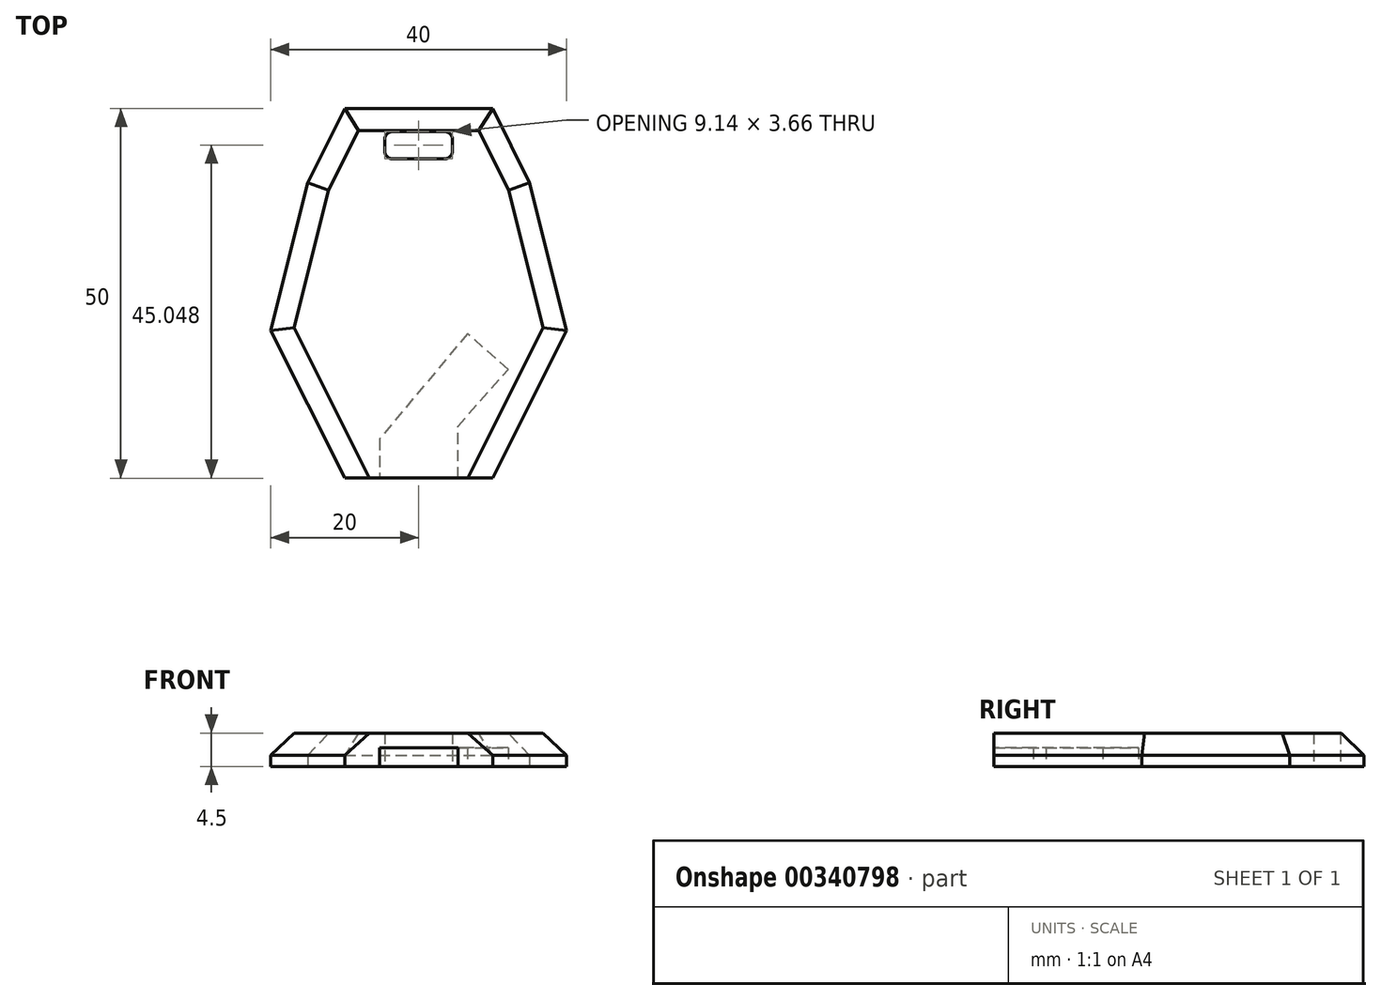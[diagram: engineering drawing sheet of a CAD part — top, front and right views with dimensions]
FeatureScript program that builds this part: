
annotation { "Feature Type Name" : "Feature", "Feature Type Description" : "" }
export const myFeature = defineFeature(function(context is Context, id is Id, definition is map)
    precondition{}
    {
        {
            var Q0;
            Q0=qCreatedBy(makeId("Top.planeOp"),FACE);
            var sketch = newSketch(context, id + "F0", { "sketchPlane" : qUnion([Q0])});
            skLineSegment(sketch, "E0", {"start": v(0, 36.91) * mm, "end": v(0, -33.24) * mm, "construction": true});
            skLineSegment(sketch, "E1", {"start": v(-15, 26.91) * mm, "end": v(15, 26.91) * mm, "construction": true});
            skLineSegment(sketch, "E2", {"start": v(-20, 6.91) * mm, "end": v(20, 6.91) * mm, "construction": true});
            skLineSegment(sketch, "E3", {"start": v(-10, 36.91) * mm, "end": v(-15, 26.91) * mm});
            skLineSegment(sketch, "E4", {"start": v(-15, 26.91) * mm, "end": v(-20, 6.91) * mm});
            skLineSegment(sketch, "E5", {"start": v(-20, 6.91) * mm, "end": v(-10, -13.09) * mm});
            skLineSegment(sketch, "E6", {"start": v(10, -13.09) * mm, "end": v(20, 6.91) * mm});
            skLineSegment(sketch, "E7", {"start": v(10, 36.91) * mm, "end": v(15, 26.91) * mm});
            skLineSegment(sketch, "E8", {"start": v(15, 26.91) * mm, "end": v(20, 6.91) * mm});
            skLineSegment(sketch, "E9", {"start": v(-10, 36.91) * mm, "end": v(10, 36.91) * mm});
            skLineSegment(sketch, "E10", {"start": v(-10, -13.09) * mm, "end": v(10, -13.09) * mm});
            skPoint(sketch, "E11", {"position": v(5.87, 6.91) * mm});
            skLineSegment(sketch, "E12", {"start": v(5.3, -13.09) * mm, "end": v(5.3, -6.09) * mm});
            skLineSegment(sketch, "E13", {"start": v(5.3, -6.09) * mm, "end": v(12.1, 1.64) * mm});
            skLineSegment(sketch, "E14", {"start": v(12.1, 1.64) * mm, "end": v(6.63, 6.47) * mm});
            skLineSegment(sketch, "E15", {"start": v(6.63, 6.47) * mm, "end": v(-5.3, -7.79) * mm});
            skLineSegment(sketch, "E16.bottom", {"start": v(-4.57, 33.79) * mm, "end": v(4.57, 33.79) * mm});
            skLineSegment(sketch, "E16.top", {"start": v(-4.57, 30.13) * mm, "end": v(4.57, 30.13) * mm});
            skLineSegment(sketch, "E16.left", {"start": v(-4.57, 33.79) * mm, "end": v(-4.57, 30.13) * mm});
            skLineSegment(sketch, "E16.right", {"start": v(4.57, 33.79) * mm, "end": v(4.57, 30.13) * mm});
            skPoint(sketch, "E16.middle", {"position": v(0, 31.96) * mm});
            skLineSegment(sketch, "E17", {"start": v(-5.3, -7.79) * mm, "end": v(-5.3, -13.09) * mm});
            skSolve(sketch);
        }
        {
            var Q0;
            Q0=makeQuery(id+"F0.imprint","IMPRINT",FACE,{"disambiguationData":[TD([[makeQuery(id+"F0.imprint","IMPRINT",EDGE,{"derivedFrom":sQuery(id+"F0.wireOp",EDGE,"E3")}),1.0]])]});
            extrude(context, id + "F1", {"entities" : qUnion([Q0]), "depth" : 4.5 * mm});
        }
        {
            var Q0;
            Q0=makeQuery(id+"F1.opExtrude","CAP_FACE",FACE,{"disambiguationData":[OSD([sQuery(id+"F0.wireOp",EDGE,"E3"),sQuery(id+"F0.wireOp",EDGE,"E4"),sQuery(id+"F0.wireOp",EDGE,"E5"),sQuery(id+"F0.wireOp",EDGE,"E6"),sQuery(id+"F0.wireOp",EDGE,"E7"),sQuery(id+"F0.wireOp",EDGE,"E8"),sQuery(id+"F0.wireOp",EDGE,"E9"),sQuery(id+"F0.wireOp",EDGE,"E10"),sQuery(id+"F0.wireOp",EDGE,"E12"),sQuery(id+"F0.wireOp",EDGE,"E13"),sQuery(id+"F0.wireOp",EDGE,"E14"),sQuery(id+"F0.wireOp",EDGE,"E15"),sQuery(id+"F0.wireOp",EDGE,"E16.bottom"),sQuery(id+"F0.wireOp",EDGE,"E16.top"),sQuery(id+"F0.wireOp",EDGE,"E16.left"),sQuery(id+"F0.wireOp",EDGE,"E16.right"),sQuery(id+"F0.wireOp",EDGE,"E17")])],"isStart":false});
            var sketch = newSketch(context, id + "F2", { "sketchPlane" : qUnion([Q0])});
            skLineSegment(sketch, "E18", {"start": v(-5.3, -13.09) * mm, "end": v(5.3, -13.09) * mm});
            skSolve(sketch);
        }
        {
            var Q0;
            Q0=makeQuery(id+"F2.imprint","IMPRINT",FACE,{"disambiguationData":[TD([[makeQuery(id+"F2.imprint","IMPRINT",EDGE,{"derivedFrom":sQuery(id+"F2.wireOp",EDGE,"E18")}),1.0]])]});
            extrude(context, id + "F3", {"entities" : qUnion([Q0]), "operationType" : NewBodyOperationType.ADD, "oppositeDirection" : true, "depth" : 2 * mm});
        }
        {
            var Q0;
            Q0=makeQuery(id+"F1.opExtrude","CAP_EDGE",EDGE,{"disambiguationData":[OSD([sQuery(id+"F0.wireOp",EDGE,"E6")])],"isStart":false});
            var Q1;
            Q1=makeQuery(id+"F1.opExtrude","CAP_EDGE",EDGE,{"disambiguationData":[OSD([sQuery(id+"F0.wireOp",EDGE,"E8")])],"isStart":false});
            var Q2;
            Q2=makeQuery(id+"F1.opExtrude","CAP_EDGE",EDGE,{"disambiguationData":[OSD([sQuery(id+"F0.wireOp",EDGE,"E5")])],"isStart":false});
            var Q3;
            Q3=makeQuery(id+"F1.opExtrude","CAP_EDGE",EDGE,{"disambiguationData":[OSD([sQuery(id+"F0.wireOp",EDGE,"E4")])],"isStart":false});
            var Q4;
            Q4=makeQuery(id+"F1.opExtrude","CAP_EDGE",EDGE,{"disambiguationData":[OSD([sQuery(id+"F0.wireOp",EDGE,"E3")])],"isStart":false});
            var Q5;
            Q5=makeQuery(id+"F1.opExtrude","CAP_EDGE",EDGE,{"disambiguationData":[OSD([sQuery(id+"F0.wireOp",EDGE,"E9")])],"isStart":false});
            var Q6;
            Q6=makeQuery(id+"F1.opExtrude","CAP_EDGE",EDGE,{"disambiguationData":[OSD([sQuery(id+"F0.wireOp",EDGE,"E7")])],"isStart":false});
            chamfer(context, id + "F4", {"entities" : qUnion([Q0, Q1, Q2, Q3, Q4, Q5, Q6]), "width" : 3 * mm, "tangentPropagation" : true});
        }
        {
            var Q0;
            Q0=makeQuery(id+"F1.opExtrude","SWEPT_EDGE",EDGE,{"disambiguationData":[OSD([sQuery(id+"F0.wireOp",EDGE,"E16.top"),sQuery(id+"F0.wireOp",EDGE,"E16.right")])]});
            var Q1;
            Q1=makeQuery(id+"F1.opExtrude","SWEPT_EDGE",EDGE,{"disambiguationData":[OSD([sQuery(id+"F0.wireOp",EDGE,"E16.top"),sQuery(id+"F0.wireOp",EDGE,"E16.left")])]});
            var Q2;
            Q2=makeQuery(id+"F1.opExtrude","SWEPT_EDGE",EDGE,{"disambiguationData":[OSD([sQuery(id+"F0.wireOp",EDGE,"E16.bottom"),sQuery(id+"F0.wireOp",EDGE,"E16.left")])]});
            var Q3;
            Q3=makeQuery(id+"F1.opExtrude","SWEPT_EDGE",EDGE,{"disambiguationData":[OSD([sQuery(id+"F0.wireOp",EDGE,"E16.bottom"),sQuery(id+"F0.wireOp",EDGE,"E16.right")])]});
            fillet(context, id + "F5", {"entities" : qUnion([Q0, Q1, Q2, Q3]), "radius" : 1 * mm, "tangentPropagation" : true, "allowEdgeOverflow" : false});
        }
    });
